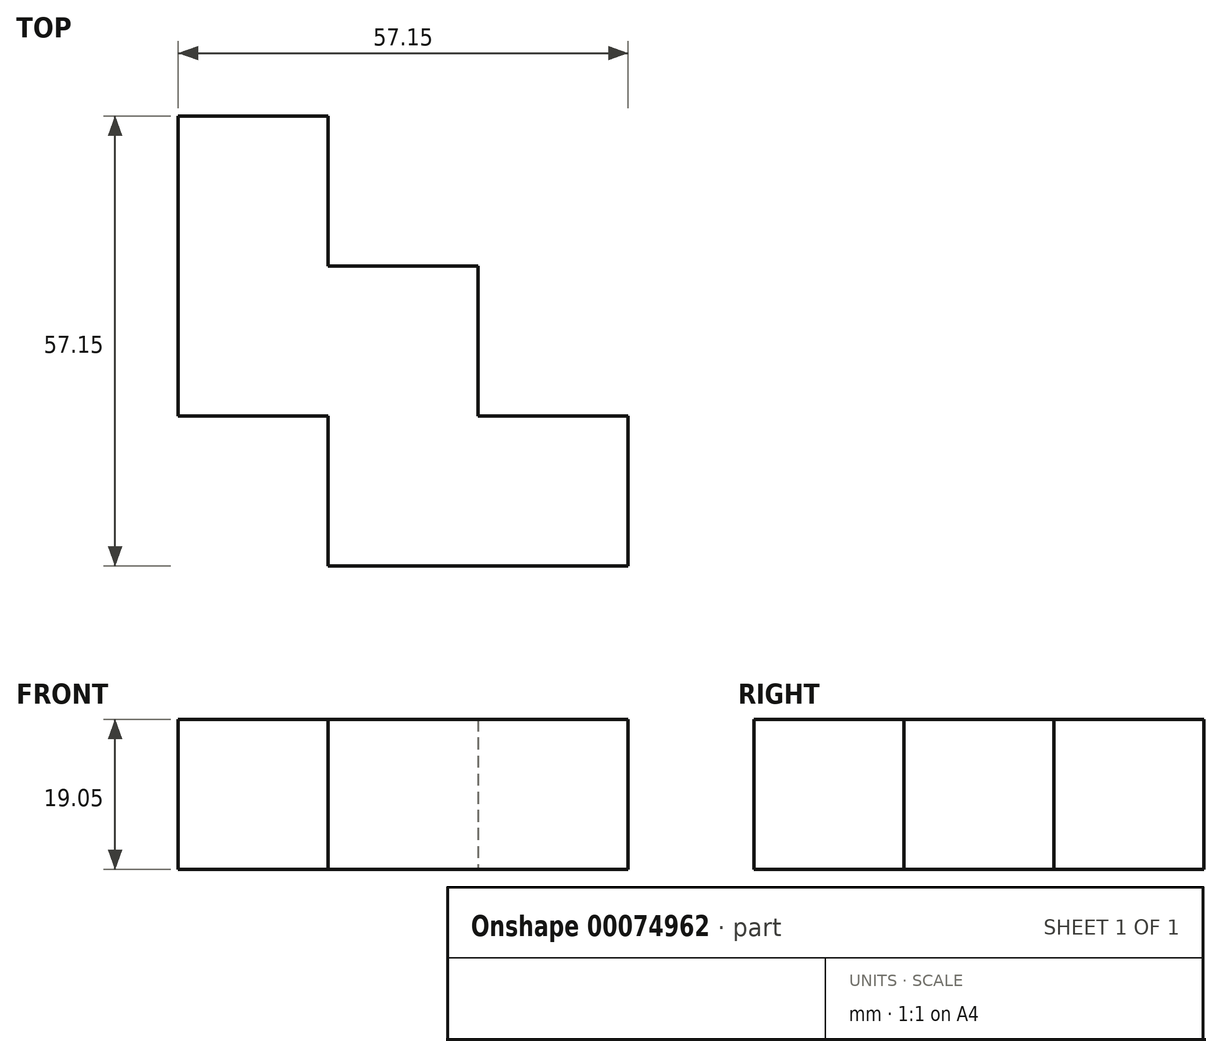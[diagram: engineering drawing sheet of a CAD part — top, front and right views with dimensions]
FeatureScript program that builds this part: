
annotation { "Feature Type Name" : "Feature", "Feature Type Description" : "" }
export const myFeature = defineFeature(function(context is Context, id is Id, definition is map)
    precondition{}
    {
        {
            var Q0;
            Q0=qCreatedBy(makeId("Top.planeOp"),FACE);
            var sketch = newSketch(context, id + "F0", { "sketchPlane" : qUnion([Q0])});
            skLineSegment(sketch, "E0", {"start": v(0, 0) * mm, "end": v(19.05, 0) * mm});
            skLineSegment(sketch, "E1", {"start": v(19.05, 0) * mm, "end": v(19.05, -19.05) * mm});
            skLineSegment(sketch, "E2", {"start": v(19.05, -19.05) * mm, "end": v(38.1, -19.05) * mm});
            skLineSegment(sketch, "E3", {"start": v(38.1, -19.05) * mm, "end": v(38.1, -38.1) * mm});
            skLineSegment(sketch, "E4", {"start": v(38.1, -38.1) * mm, "end": v(57.15, -38.1) * mm});
            skLineSegment(sketch, "E5", {"start": v(57.15, -38.1) * mm, "end": v(57.15, -57.15) * mm});
            skLineSegment(sketch, "E6", {"start": v(57.15, -57.15) * mm, "end": v(19.05, -57.15) * mm});
            skLineSegment(sketch, "E7", {"start": v(19.05, -57.15) * mm, "end": v(19.05, -38.1) * mm});
            skLineSegment(sketch, "E8", {"start": v(19.05, -38.1) * mm, "end": v(0, -38.1) * mm});
            skLineSegment(sketch, "E9", {"start": v(0, -38.1) * mm, "end": v(0, 0) * mm});
            skSolve(sketch);
        }
        {
            var Q0;
            Q0 = qSketchRegion(id + "F0", true);
            extrude(context, id + "F1", {"entities" : qUnion([Q0]), "depth" : 19.05 * mm});
        }
    });
